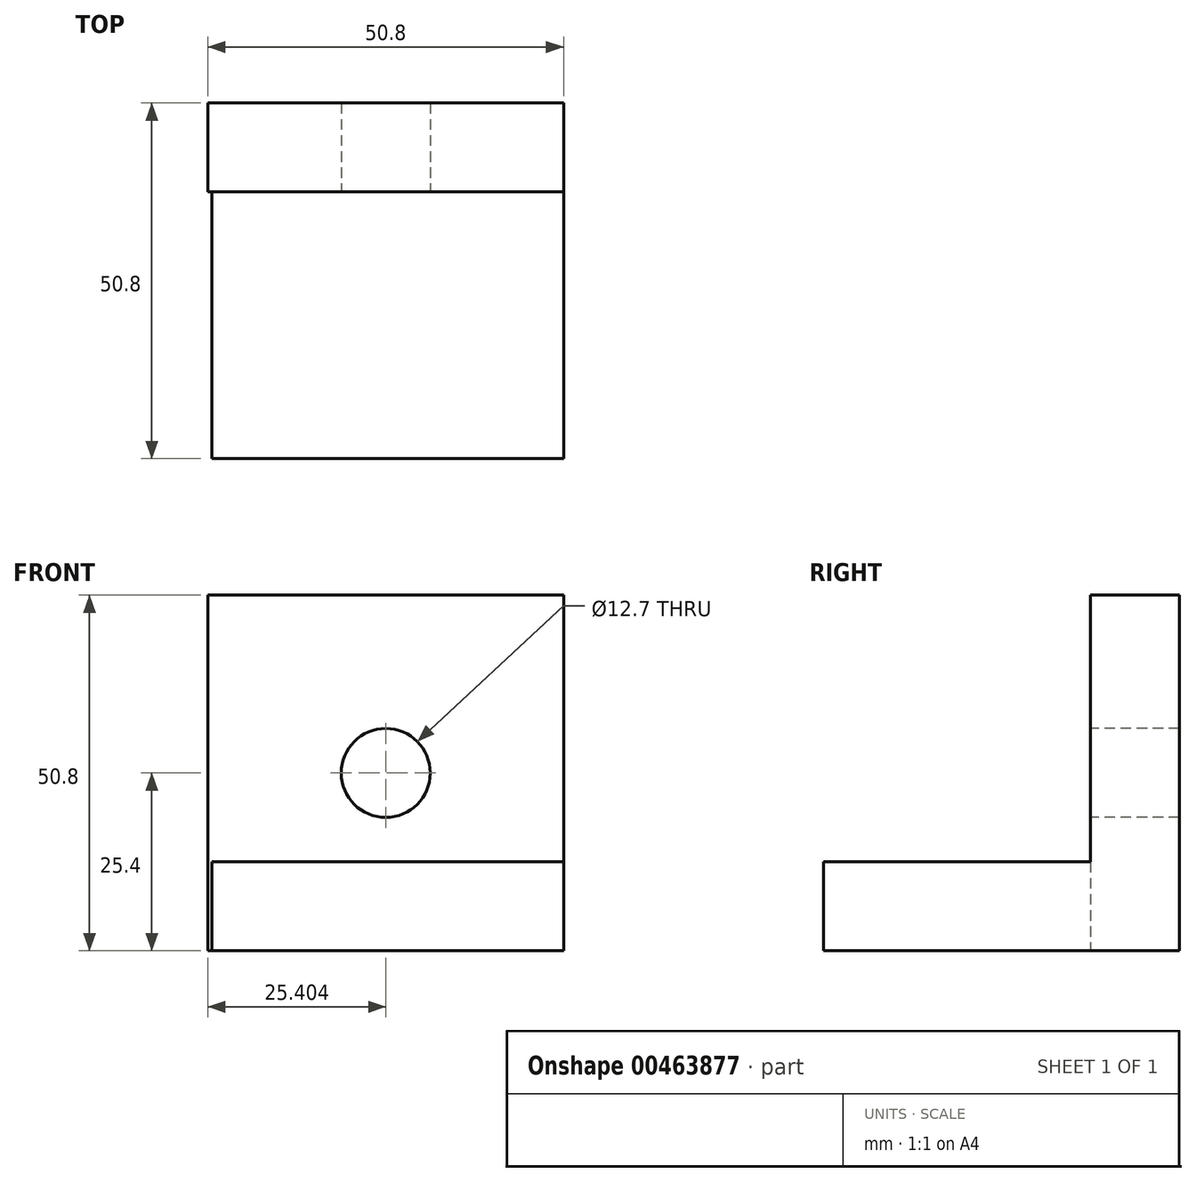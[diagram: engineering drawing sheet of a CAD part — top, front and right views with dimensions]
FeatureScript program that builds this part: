
annotation { "Feature Type Name" : "Feature", "Feature Type Description" : "" }
export const myFeature = defineFeature(function(context is Context, id is Id, definition is map)
    precondition{}
    {
        {
            var Q0;
            Q0=qCreatedBy(makeId("Front.planeOp"),FACE);
            var sketch = newSketch(context, id + "F0", { "sketchPlane" : qUnion([Q0])});
            skLineSegment(sketch, "E0", {"start": v(-26.13, 0) * mm, "end": v(24.67, 0) * mm});
            skLineSegment(sketch, "E1", {"start": v(-26.13, 0) * mm, "end": v(-26.13, 50.8) * mm});
            skLineSegment(sketch, "E2", {"start": v(24.67, 0) * mm, "end": v(24.67, 50.8) * mm});
            skLineSegment(sketch, "E3", {"start": v(24.67, 50.8) * mm, "end": v(-26.13, 50.8) * mm});
            skSolve(sketch);
        }
        {
            var Q0;
            Q0 = qSketchRegion(id + "F0", true);
            extrude(context, id + "F1", {"entities" : qUnion([Q0]), "depth" : 12.7 * mm});
        }
        {
            var Q0;
            Q0=makeQuery(id+"F1.opExtrude","CAP_FACE",FACE,{"disambiguationData":[OSD([sQuery(id+"F0.wireOp",EDGE,"E0"),sQuery(id+"F0.wireOp",EDGE,"E1"),sQuery(id+"F0.wireOp",EDGE,"E2"),sQuery(id+"F0.wireOp",EDGE,"E3")])],"isStart":false});
            var sketch = newSketch(context, id + "F2", { "sketchPlane" : qUnion([Q0])});
            skCircle(sketch, "E4", {"center": v(-0.73, 25.4) * mm, "radius": 6.35 * mm});
            skPoint(sketch, "E4.centerSnap0", {"position": v(-26.13, 25.4) * mm});
            skPoint(sketch, "E4.centerSnap1", {"position": v(-0.73, 50.8) * mm});
            skSolve(sketch);
        }
        {
            var Q0;
            Q0=makeQuery(id+"F2.imprint","IMPRINT",FACE,{"disambiguationData":[TD([[makeQuery(id+"F2.imprint","IMPRINT",EDGE,{"derivedFrom":sQuery(id+"F2.wireOp",EDGE,"E4")}),-1.0]])]});
            var sketch = newSketch(context, id + "F3", { "sketchPlane" : qUnion([Q0])});
            skLineSegment(sketch, "E5", {"start": v(-25.57, 0) * mm, "end": v(25.23, 0) * mm});
            skLineSegment(sketch, "E6", {"start": v(25.23, 0) * mm, "end": v(25.23, 12.7) * mm});
            skLineSegment(sketch, "E7", {"start": v(25.23, 12.7) * mm, "end": v(-25.57, 12.7) * mm});
            skLineSegment(sketch, "E8", {"start": v(-25.57, 12.7) * mm, "end": v(-25.57, 0) * mm});
            skSolve(sketch);
        }
        {
            var Q0;
            {var subQ0=sQuery(id+"F3.wireOp",EDGE,"E8");Q0=makeQuery(id+"F3.imprint","IMPRINT",FACE,{"disambiguationData":[TD([[makeQuery(id+"F3.imprint","IMPRINT",EDGE,{"derivedFrom":subQ0}),1.0]])]});}
            extrude(context, id + "F4", {"entities" : qUnion([Q0]), "operationType" : NewBodyOperationType.ADD, "depth" : 38.1 * mm});
        }
        {
            var Q0;
            Q0=makeQuery(id+"F2.imprint","IMPRINT",FACE,{"disambiguationData":[TD([[makeQuery(id+"F2.imprint","IMPRINT",EDGE,{"derivedFrom":sQuery(id+"F2.wireOp",EDGE,"E4")}),1.0]])]});
            extrude(context, id + "F5", {"entities" : qUnion([Q0]), "operationType" : NewBodyOperationType.REMOVE, "oppositeDirection" : true, "depth" : 25.4 * mm});
        }
    });
